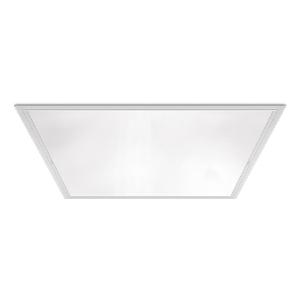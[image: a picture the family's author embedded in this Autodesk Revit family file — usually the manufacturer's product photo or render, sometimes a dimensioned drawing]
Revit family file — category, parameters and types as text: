
# Revit family: 3f_filippi_-_l_600_luce_diffusa_lgs_3f_filippi_-_22822_-_l_600_42w-840_dali_lgs_596x596
name_source: partatom
category: Lighting Fixtures
units: mm (PartAtom-declared; Revit-internal decimal feet)

## family parameters
Cut with Voids When Loaded = No
Host = Face
Light Source = No
Part Type = Normal
Room Calculation Point = No
Round Connector Dimension = Use Diameter
Shared = No

## types (1)
- 3F Filippi - L 600 Luce Diffusa LGS (1 x LED, 5776 lm, 45 W, 4000 K)
    Apparent Load = 45 VA
    Approval mark = ENEC
    CIE Flux Codes = 66 93 98 100 100
    Color Rendering = 80
    Color Temperature = 4000 K
    Control Gear = Electronic transformer
    Default Elevation = 1800 mm
    Description = ILLUMINOTECHNICAL
Luminous efficiency 100% (DLOR 100%, ULOR 0%).
Initial luminous flux of the luminaire 5776 lm.
Direct symmetric distribution.
Installation Interdistance Transv.D = 1.14 x hu - Long.D = 1.16 x hu.
Average luminance <3000 cd/m² for radial angles >65°.
Tabular UGR (CIE 117 - 4H-8H; S=0.25H; 70/50/20): RUG 17.9 - 17.8.
Beam angle: 85° - 85°.
Luminous efficacy 128 lm/W.
Lifetime (L93/B10): 30000 h. (tq+25°C)
Lifetime (L90/B10): 50000 h. (tq+25°C)
Lifetime (L85/B10): 80000 h. (tq+25°C)
Lifetime (L80/B10): 100000 h. (tq+25°C)
Sudden decreased luminous flux after 50000 hours: 0% (C0).
Photobiological safety in compliance with IEC/TR 62778: RG0 risk exempt, (IEC 62471).
In compliance with IEC/EN 62722-2-1 - IEC/EN 62717 standards.

SOURCE
Squared LED module 42W/840.
Source with special protection against aggressive chemically-volatile substances for standard LED technology.
Energy efficiency class (UE 2019/2020 - UE 2019/2015): D.
CIE 13.3 Colour rendering index: CRI >80 (R9 <50%).
IES TM-30 Fidelity Index: Rf = 84 Rg = 95.
CCT nominal colour temperature 4000 K.
Colour initial tolerance (MacAdam): SDCM 3.

MECHANICAL
Housing in galvannealed steel, painted in white epoxy-polyester.
Perimetral frame in white polycarbonate.
LGS micro-prismatic flat diffuser in transparent methacrylate (PMMA), multi-lenticular exterior, anti-glare.
Anti-glare opal polycarbonate filter for brightness uniformity.
Luminaire with limited surface temperature. - D - (EN 60598-2-24)
Dimensions: 596x596 mm, height 95 mm. Weight 5.32 kg.
IP65 protection degree for exposed part, IP64 for recessed part.
Mechanical strength to impacts IK06 (1 joule).
Glow-wire test resistance 650°C.

ELECTRICAL
Halogen Free DALI-2, PUSH-DIM, electronic wiring 230V-50/60Hz, power factor 0.95 at full load, THD <25%, constant output current, class I, 1 driver, 1 DALI addresse.
Power of the luminaire 45 W.
CE - IEC 60598-1 - EN 60598-1.
SAFE FLICKER: PstLM=<1 and SVM=<0.4 (IEC TR 61547-1 and IEC TR 63158), to ensure a more comfortable and safe light.
Luminaire compliant with EN 60598-2-22 for power supply from a centralised emergency system CPSS (Central Power Supply System), not incorporated in the luminaire - high risk areas excluded. The default power and flux are 100% in AC and 15% in DC.
Ambient temperature from 0°C to +40°C.
Temperature class T6 max 85°C.
5-pole terminal block (L-N-PE-DA/DA) quick connection for line connection with connection capacity 2x2.5 mm² per poles.
Relative humidity UR: <85%.

INSTALLATION
Lay-on or pull-up recessed fitting using frame accessory.
All accessories dedicated to this product are available on the Catalog and on our website www.3F-Filippi.com.

APPLICATIONS
Suitable product for food production plants (HACCP), IFS (Food Version 6), BRC (GSFS Food Version 7).
In environments requiring protection and simplified cleaning.
Hospitals, pharmaceutical, chemical, aseptic laboratories, sterilised rooms.
Environments with VDTs.
Environments where demanding visual tasks are performed and soft diffuse light is required for optimal visual comfort and total shielding of the light source.

LIGHT MANAGEMENT
Recommended minimum setting: 10%.
The device, equipped with DALI-2 driver, can be controlled manually with 3F Easy Dim technology or automatically/manually with 3F Smart Dimming technology and/or centralised DALI systems.
DALI-2 certification guarantees interoperability with other devices with the same certification.
In electrical systems without a regulation system (manual or automatic) and DALI bus, a suitable jumper must be made on the DA-DA terminals of the appliance.

WARNING
Luminaire designed for disposal/recycling at end-of-life.
Replaceable (LED only) light source by a professional. Replaceable control gear by a professional.
    Height = 0 mm  [stored 0 ft]
    Lamp = 1 x LED
    Lamp Light Flux = 5776 lm
    Lamp Power = 45 W
    Lamp count = 1
    Length = 596 mm
    Lifetime = 50000 h
    Luminous efficacy = 128 lm/W
    Manufacturer = 3F Filippi
    ModVariant = No
    Model = 3F Filippi - 22822 - L 600 42W-840 DALI LGS 596x596
    Mounting Place = Ceiling
    Mounting Type = Recessed
    Number of Poles = 1
    OnlyDefault = Yes
    Power Factor = 1
    Product Name = 3F Filippi - L 600 Luce Diffusa LGS
    Product group = recessed luminaire
    ProductGroupID = 4
    Protection Class = Protection class I
    Protection Degree = IP 64
    RLX_Detail_Level = 1
    RLX_Emergency_Light_Flux = 0 lm
    RLX_Emergency_Type = 0
    RLX_Emergency_Type_DB = No
    RlxData = <blob elided: 129821 chars, md5=2e4f7277>
    Socket = socket
    Standby Power = 0 W
    System Light Flux = 5776 lm
    System Power = 45 W
    Type Comments = Product without accessories
    Type Image = 3ffilippi_l_600_luce_diffusa_lgs.jpg
    URL = http://relux.com
    VarID = ---
    Voltage = 0 V
    Weight = 0.00 kg
    Width = 596 mm

note: [stored X ft] marks values corroborated as IEEE doubles in the binary element streams (Revit-internal decimal feet)

## geometry (parser evidence)
native form markers: Blend x4, Sweep x9
no freeform markers — native parametric forms only
